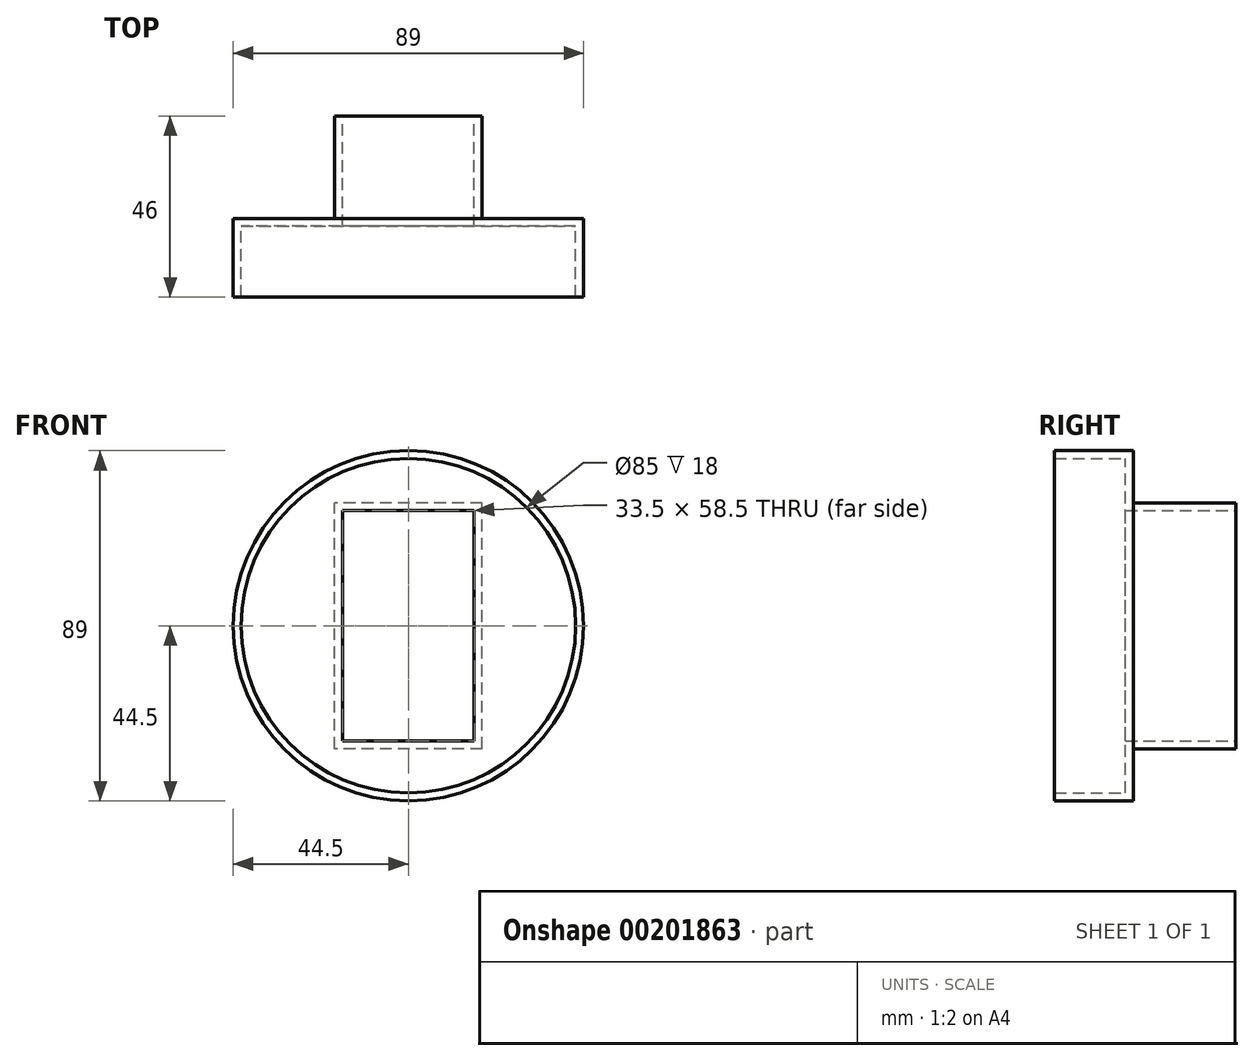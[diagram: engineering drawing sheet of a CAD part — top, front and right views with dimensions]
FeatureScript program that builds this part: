
annotation { "Feature Type Name" : "Feature", "Feature Type Description" : "" }
export const myFeature = defineFeature(function(context is Context, id is Id, definition is map)
    precondition{}
    {
        {
            var Q0;
            Q0=qCreatedBy(makeId("Front.planeOp"),FACE);
            var sketch = newSketch(context, id + "F0", { "sketchPlane" : qUnion([Q0])});
            skLineSegment(sketch, "E0.bottom", {"start": v(0, 0) * mm, "end": v(-37.5, 0) * mm});
            skLineSegment(sketch, "E0.top", {"start": v(0, 62.5) * mm, "end": v(-37.5, 62.5) * mm});
            skLineSegment(sketch, "E0.left", {"start": v(0, 0) * mm, "end": v(0, 62.5) * mm});
            skLineSegment(sketch, "E0.right", {"start": v(-37.5, 0) * mm, "end": v(-37.5, 62.5) * mm});
            skSolve(sketch);
        }
        {
            var Q0;
            Q0=makeQuery(id+"F0.imprint","IMPRINT",FACE,{"disambiguationData":[TD([[makeQuery(id+"F0.imprint","IMPRINT",EDGE,{"derivedFrom":sQuery(id+"F0.wireOp",EDGE,"E0.bottom")}),-1.0]])]});
            extrude(context, id + "F1", {"entities" : qUnion([Q0]), "depth" : 26 * mm});
        }
        {
            var Q0;
            Q0=makeQuery(id+"F1.opExtrude","CAP_FACE",FACE,{"disambiguationData":[OSD([sQuery(id+"F0.wireOp",EDGE,"E0.bottom"),sQuery(id+"F0.wireOp",EDGE,"E0.top"),sQuery(id+"F0.wireOp",EDGE,"E0.left"),sQuery(id+"F0.wireOp",EDGE,"E0.right")])],"isStart":false});
            var sketch = newSketch(context, id + "F2", { "sketchPlane" : qUnion([Q0])});
            skCircle(sketch, "E1", {"center": v(-18.75, 31.25) * mm, "radius": 44.5 * mm});
            skPoint(sketch, "E1.centerSnap0", {"position": v(-18.75, 62.5) * mm});
            skPoint(sketch, "E1.centerSnap1", {"position": v(-37.5, 31.25) * mm});
            skSolve(sketch);
        }
        {
            var Q0;
            Q0=makeQuery(id+"F2.imprint","IMPRINT",FACE,{"disambiguationData":[TD([[makeQuery(id+"F2.imprint","IMPRINT",EDGE,{"derivedFrom":sQuery(id+"F2.wireOp",EDGE,"E1")}),1.0]])]});
            var Q1;
            Q1=makeQuery(id+"F2.imprint","IMPRINT",FACE,{"disambiguationData":[TD([[makeQuery(id+"F2.imprint","IMPRINT",EDGE,{"derivedFrom":makeQuery(id+"F1.opExtrude","CAP_EDGE",EDGE,{"disambiguationData":[OSD([sQuery(id+"F0.wireOp",EDGE,"E0.bottom")])],"isStart":false})}),-1.0]])]});
            extrude(context, id + "F3", {"entities" : qUnion([Q0, Q1]), "operationType" : NewBodyOperationType.ADD, "depth" : 20 * mm});
        }
        {
            var Q0;
            Q0=makeQuery(id+"F3.opExtrude","CAP_FACE",FACE,{"disambiguationData":[OSD([sQuery(id+"F2.wireOp",EDGE,"E1")])],"isStart":false});
            var Q1;
            Q1=makeQuery(id+"F1.opExtrude","CAP_FACE",FACE,{"disambiguationData":[OSD([sQuery(id+"F0.wireOp",EDGE,"E0.bottom"),sQuery(id+"F0.wireOp",EDGE,"E0.top"),sQuery(id+"F0.wireOp",EDGE,"E0.left"),sQuery(id+"F0.wireOp",EDGE,"E0.right")])],"isStart":true});
            shell(context, id + "F4", {"entities" : qUnion([Q0, Q1]), "thickness" : 2 * mm});
        }
    });
